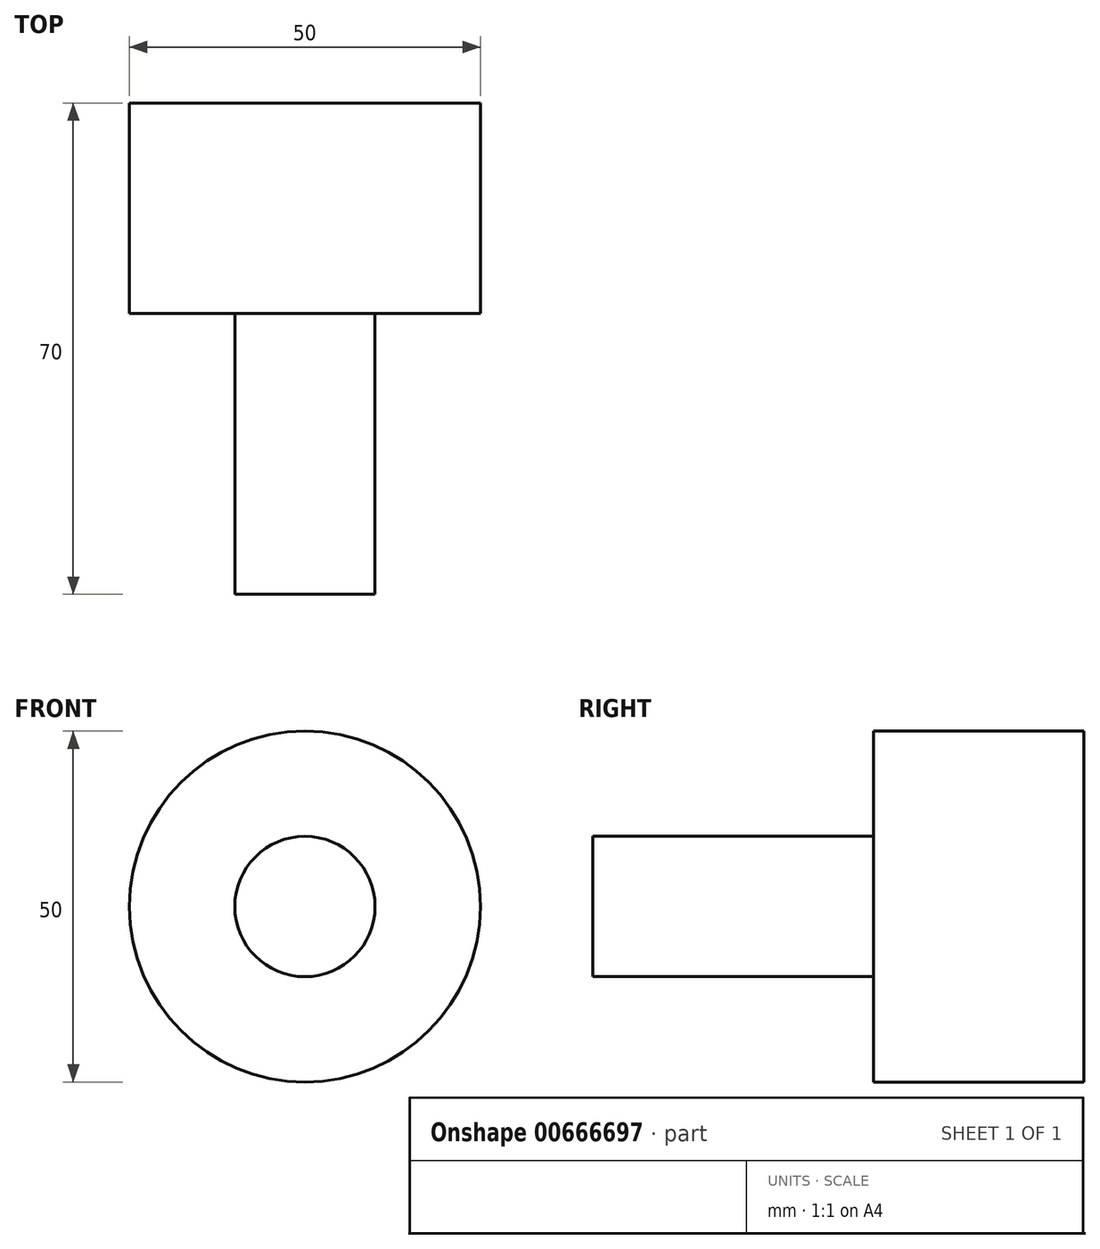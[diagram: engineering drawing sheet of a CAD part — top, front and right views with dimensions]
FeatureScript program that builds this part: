
annotation { "Feature Type Name" : "Feature", "Feature Type Description" : "" }
export const myFeature = defineFeature(function(context is Context, id is Id, definition is map)
    precondition{}
    {
        {
            var Q0;
            Q0=qCreatedBy(makeId("Front.planeOp"),FACE);
            var sketch = newSketch(context, id + "F0", { "sketchPlane" : qUnion([Q0])});
            skCircle(sketch, "E0", {"center": v(0, 0) * mm, "radius": 25 * mm});
            skSolve(sketch);
        }
        {
            var Q0;
            Q0=makeQuery(id+"F0.imprint","IMPRINT",FACE,{"disambiguationData":[TD([[makeQuery(id+"F0.imprint","IMPRINT",EDGE,{"derivedFrom":sQuery(id+"F0.wireOp",EDGE,"E0")}),1.0]])]});
            extrude(context, id + "F1", {"entities" : qUnion([Q0]), "oppositeDirection" : true, "depth" : 30 * mm, "offsetDistance" : 25 * mm});
        }
        {
            var Q0;
            Q0=makeQuery(id+"F1.opExtrude","CAP_FACE",FACE,{"disambiguationData":[OSD([sQuery(id+"F0.wireOp",EDGE,"E0")])],"isStart":true});
            var sketch = newSketch(context, id + "F2", { "sketchPlane" : qUnion([Q0])});
            skCircle(sketch, "E1", {"center": v(0, 0) * mm, "radius": 10 * mm});
            skSolve(sketch);
        }
        {
            var Q0;
            Q0=makeQuery(id+"F2.imprint","IMPRINT",FACE,{"disambiguationData":[TD([[makeQuery(id+"F2.imprint","IMPRINT",EDGE,{"derivedFrom":sQuery(id+"F2.wireOp",EDGE,"E1")}),1.0]])]});
            extrude(context, id + "F3", {"entities" : qUnion([Q0]), "operationType" : NewBodyOperationType.ADD, "depth" : 40 * mm, "offsetDistance" : 25 * mm});
        }
    });
